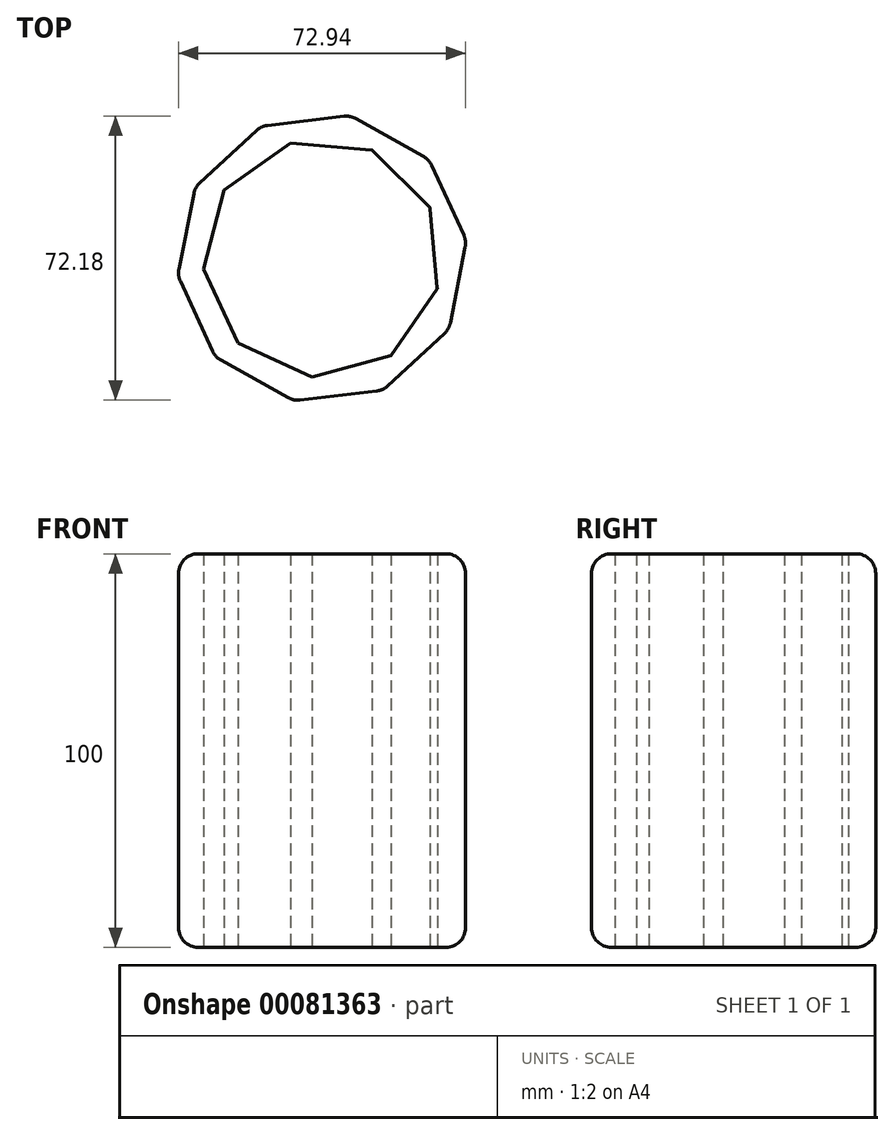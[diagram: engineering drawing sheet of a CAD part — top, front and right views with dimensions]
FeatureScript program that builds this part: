
annotation { "Feature Type Name" : "Feature", "Feature Type Description" : "" }
export const myFeature = defineFeature(function(context is Context, id is Id, definition is map)
    precondition{}
    {
        {
            var Q0;
            Q0=qCreatedBy(makeId("Top.planeOp"),FACE);
            var sketch = newSketch(context, id + "F0", { "sketchPlane" : qUnion([Q0])});
            skCircle(sketch, "E0.cCircle", {"center": v(0, 0) * mm, "radius": 35.14 * mm, "construction": true});
            skLineSegment(sketch, "E0.0", {"start": v(7.18, 36.24) * mm, "end": v(27.11, 25.1) * mm});
            skLineSegment(sketch, "E0.1", {"start": v(27.11, 25.1) * mm, "end": v(36.69, 4.37) * mm});
            skLineSegment(sketch, "E0.2", {"start": v(36.69, 4.37) * mm, "end": v(32.25, -18.03) * mm});
            skLineSegment(sketch, "E0.3", {"start": v(32.25, -18.03) * mm, "end": v(15.5, -33.54) * mm});
            skLineSegment(sketch, "E0.4", {"start": v(15.5, -33.54) * mm, "end": v(-7.18, -36.24) * mm});
            skLineSegment(sketch, "E0.5", {"start": v(-7.18, -36.24) * mm, "end": v(-27.11, -25.1) * mm});
            skLineSegment(sketch, "E0.6", {"start": v(-27.11, -25.1) * mm, "end": v(-36.69, -4.37) * mm});
            skLineSegment(sketch, "E0.7", {"start": v(-36.69, -4.37) * mm, "end": v(-32.25, 18.03) * mm});
            skLineSegment(sketch, "E0.8", {"start": v(-32.25, 18.03) * mm, "end": v(-15.5, 33.54) * mm});
            skLineSegment(sketch, "E0.9", {"start": v(-15.5, 33.54) * mm, "end": v(7.18, 36.24) * mm});
            skPoint(sketch, "E0.0.midPoint", {"position": v(17.15, 30.67) * mm});
            skCircle(sketch, "E1.cCircle", {"center": v(0, 0) * mm, "radius": 28.44 * mm, "construction": true});
            skLineSegment(sketch, "E1.0", {"start": v(-7.96, 29.2) * mm, "end": v(12.68, 27.49) * mm});
            skLineSegment(sketch, "E1.1", {"start": v(12.68, 27.49) * mm, "end": v(27.38, 12.9) * mm});
            skLineSegment(sketch, "E1.2", {"start": v(27.38, 12.9) * mm, "end": v(29.27, -7.7) * mm});
            skLineSegment(sketch, "E1.3", {"start": v(29.27, -7.7) * mm, "end": v(17.47, -24.72) * mm});
            skLineSegment(sketch, "E1.4", {"start": v(17.47, -24.72) * mm, "end": v(-2.5, -30.17) * mm});
            skLineSegment(sketch, "E1.5", {"start": v(-2.5, -30.17) * mm, "end": v(-21.31, -21.5) * mm});
            skLineSegment(sketch, "E1.6", {"start": v(-21.31, -21.5) * mm, "end": v(-30.14, -2.77) * mm});
            skLineSegment(sketch, "E1.7", {"start": v(-30.14, -2.77) * mm, "end": v(-24.87, 17.26) * mm});
            skLineSegment(sketch, "E1.8", {"start": v(-24.87, 17.26) * mm, "end": v(-7.96, 29.2) * mm});
            skPoint(sketch, "E1.0.midPoint", {"position": v(2.36, 28.35) * mm});
            skSolve(sketch);
        }
        {
            var Q0;
            Q0=makeQuery(id+"F0.imprint","IMPRINT",FACE,{"disambiguationData":[TD([[makeQuery(id+"F0.imprint","IMPRINT",EDGE,{"derivedFrom":sQuery(id+"F0.wireOp",EDGE,"E0.0")}),-1.0]])]});
            extrude(context, id + "F1", {"entities" : qUnion([Q0]), "depth" : 100 * mm});
        }
        {
            var Q0;
            Q0=makeQuery(id+"F1.opExtrude","SWEPT_FACE",FACE,{"disambiguationData":[OSD([sQuery(id+"F0.wireOp",EDGE,"E0.4")])]});
            var Q1;
            Q1=makeQuery(id+"F1.opExtrude","SWEPT_FACE",FACE,{"disambiguationData":[OSD([sQuery(id+"F0.wireOp",EDGE,"E0.3")])]});
            var Q2;
            Q2=makeQuery(id+"F1.opExtrude","SWEPT_FACE",FACE,{"disambiguationData":[OSD([sQuery(id+"F0.wireOp",EDGE,"E0.2")])]});
            var Q3;
            Q3=makeQuery(id+"F1.opExtrude","SWEPT_FACE",FACE,{"disambiguationData":[OSD([sQuery(id+"F0.wireOp",EDGE,"E0.5")])]});
            var Q4;
            Q4=makeQuery(id+"F1.opExtrude","SWEPT_FACE",FACE,{"disambiguationData":[OSD([sQuery(id+"F0.wireOp",EDGE,"E0.6")])]});
            var Q5;
            Q5=makeQuery(id+"F1.opExtrude","SWEPT_FACE",FACE,{"disambiguationData":[OSD([sQuery(id+"F0.wireOp",EDGE,"E0.7")])]});
            var Q6;
            Q6=makeQuery(id+"F1.opExtrude","SWEPT_FACE",FACE,{"disambiguationData":[OSD([sQuery(id+"F0.wireOp",EDGE,"E0.8")])]});
            var Q7;
            Q7=makeQuery(id+"F1.opExtrude","SWEPT_FACE",FACE,{"disambiguationData":[OSD([sQuery(id+"F0.wireOp",EDGE,"E0.9")])]});
            var Q8;
            Q8=makeQuery(id+"F1.opExtrude","SWEPT_FACE",FACE,{"disambiguationData":[OSD([sQuery(id+"F0.wireOp",EDGE,"E0.0")])]});
            var Q9;
            Q9=makeQuery(id+"F1.opExtrude","SWEPT_FACE",FACE,{"disambiguationData":[OSD([sQuery(id+"F0.wireOp",EDGE,"E0.1")])]});
            fillet(context, id + "F2", {"entities" : qUnion([Q0, Q1, Q2, Q3, Q4, Q5, Q6, Q7, Q8, Q9]), "radius" : 5 * mm, "tangentPropagation" : true, "allowEdgeOverflow" : false});
        }
    });
